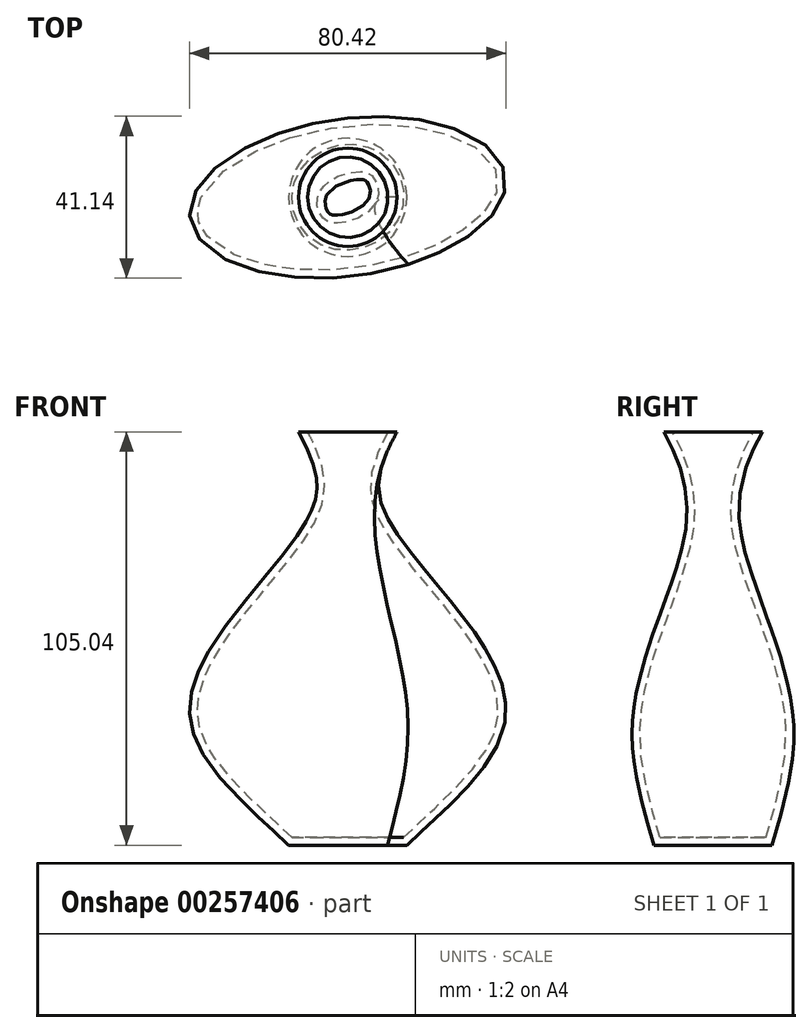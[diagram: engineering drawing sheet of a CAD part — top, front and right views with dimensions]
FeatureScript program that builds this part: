
annotation { "Feature Type Name" : "Feature", "Feature Type Description" : "" }
export const myFeature = defineFeature(function(context is Context, id is Id, definition is map)
    precondition{}
    {
        {
            var Q0;
            Q0=qCreatedBy(makeId("Top.planeOp"),FACE);
            var sketch = newSketch(context, id + "F0", { "sketchPlane" : qUnion([Q0])});
            skEllipse(sketch, "E0", {"center": v(0, 0) * mm, "majorRadius": 12.5 * mm, "minorRadius": 12.5 * mm, "majorAxis": v(1, 0)});
            skSolve(sketch);
        }
        {
            var Q0;
            Q0=qCreatedBy(makeId("Top.planeOp"),FACE);
            cPlane(context, id + "F1", {"entities" : qUnion([Q0]), "cplaneType" : CPlaneType.OFFSET, "offset" : 5 * mm, "oppositeDirection" : true, "width" : 150 * mm, "height" : 150 * mm});
        }
        {
            var Q0;
            Q0=qCreatedBy(id+"F1.planeOp",FACE);
            var sketch = newSketch(context, id + "F2", { "sketchPlane" : qUnion([Q0])});
            skCircle(sketch, "E1.0.0", {"center": v(0, 0) * mm, "radius": 12.5 * mm, "construction": true});
            skCircle(sketch, "E2", {"center": v(0, 0) * mm, "radius": 10 * mm});
            skSolve(sketch);
        }
        {
            var Q0;
            Q0=qCreatedBy(id+"F1.planeOp",FACE);
            cPlane(context, id + "F3", {"entities" : qUnion([Q0]), "cplaneType" : CPlaneType.OFFSET, "offset" : 70 * mm, "oppositeDirection" : true, "width" : 150 * mm, "height" : 150 * mm});
        }
        {
            var Q0;
            Q0=qCreatedBy(id+"F3.planeOp",FACE);
            var sketch = newSketch(context, id + "F4", { "sketchPlane" : qUnion([Q0])});
            skCircle(sketch, "E3.0.0", {"center": v(0, 0) * mm, "radius": 10 * mm, "construction": true});
            skEllipse(sketch, "E4", {"center": v(0, 0) * mm, "majorRadius": 40 * mm, "minorRadius": 20 * mm, "majorAxis": v(1, 0.13)});
            skSolve(sketch);
        }
        {
            var Q0;
            Q0=qCreatedBy(id+"F3.planeOp",FACE);
            cPlane(context, id + "F5", {"entities" : qUnion([Q0]), "cplaneType" : CPlaneType.OFFSET, "offset" : 30 * mm, "oppositeDirection" : true, "width" : 150 * mm, "height" : 150 * mm});
        }
        {
            var Q0;
            Q0=qCreatedBy(id+"F5.planeOp",FACE);
            var sketch = newSketch(context, id + "F6", { "sketchPlane" : qUnion([Q0])});
            skEllipse(sketch, "E5.0.0", {"center": v(0, 0) * mm, "majorRadius": 40 * mm, "minorRadius": 20 * mm, "majorAxis": v(1, 0.13), "construction": true});
            skCircle(sketch, "E6", {"center": v(0, 0) * mm, "radius": 15 * mm});
            skSolve(sketch);
        }
        {
            var Q0;
            Q0=makeQuery(id+"F0.imprint","IMPRINT",FACE,{"disambiguationData":[TD([[makeQuery(id+"F0.imprint","IMPRINT",EDGE,{"derivedFrom":sQuery(id+"F0.wireOp",EDGE,"E0")}),1.0]])]});
            var Q1;
            Q1=makeQuery(id+"F2.imprint","IMPRINT",FACE,{"disambiguationData":[TD([[makeQuery(id+"F2.imprint","IMPRINT",EDGE,{"derivedFrom":sQuery(id+"F2.wireOp",EDGE,"E2")}),1.0]])]});
            var Q2;
            Q2=makeQuery(id+"F4.imprint","IMPRINT",FACE,{"disambiguationData":[TD([[makeQuery(id+"F4.imprint","IMPRINT",EDGE,{"derivedFrom":sQuery(id+"F4.wireOp",EDGE,"E4")}),1.0]])]});
            var Q3;
            Q3=makeQuery(id+"F6.imprint","IMPRINT",FACE,{"disambiguationData":[TD([[makeQuery(id+"F6.imprint","IMPRINT",EDGE,{"derivedFrom":sQuery(id+"F6.wireOp",EDGE,"E6")}),1.0]])]});
            loft(context, id + "F7", {"sheetProfilesArray" : [{ "sheetProfileEntities" : qUnion([Q0]) }, { "sheetProfileEntities" : qUnion([Q1]) }, { "sheetProfileEntities" : qUnion([Q2]) }, { "sheetProfileEntities" : qUnion([Q3]) }]});
        }
        {
            var Q0;
            Q0=makeQuery(id+"F7.opLoft","CAP_FACE",FACE,{"disambiguationData":[OSD([makeQuery(id+"F0.imprint","IMPRINT",FACE,{"disambiguationData":[TD([[makeQuery(id+"F0.imprint","IMPRINT",EDGE,{"derivedFrom":sQuery(id+"F0.wireOp",EDGE,"E0")}),1.0]])]})])],"isStart":true});
            shell(context, id + "F8", {"entities" : qUnion([Q0]), "thickness" : 2 * mm});
        }
    });
